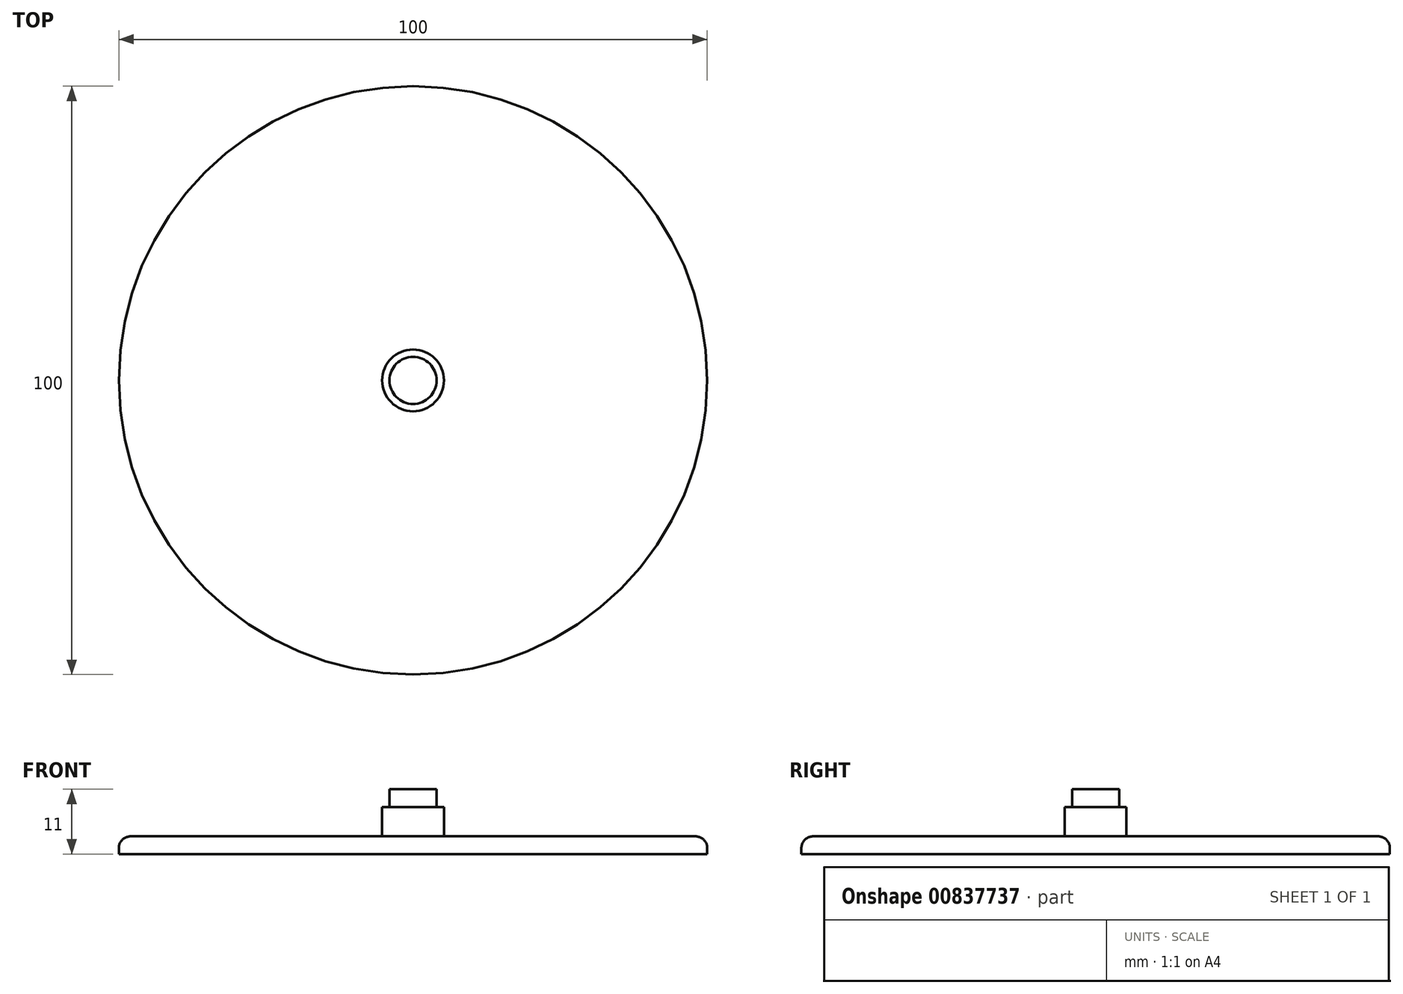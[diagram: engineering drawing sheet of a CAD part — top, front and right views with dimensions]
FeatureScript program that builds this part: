
annotation { "Feature Type Name" : "Feature", "Feature Type Description" : "" }
export const myFeature = defineFeature(function(context is Context, id is Id, definition is map)
    precondition{}
    {
        {
            var Q0;
            Q0=qCreatedBy(makeId("Top.planeOp"),FACE);
            var sketch = newSketch(context, id + "F0", { "sketchPlane" : qUnion([Q0])});
            skCircle(sketch, "E0", {"center": v(0, 0) * mm, "radius": 50 * mm});
            skCircle(sketch, "E1", {"center": v(0, 0) * mm, "radius": 5.25 * mm});
            skCircle(sketch, "E2", {"center": v(0, 0) * mm, "radius": 4 * mm});
            skSolve(sketch);
        }
        {
            var Q0;
            Q0=makeQuery(id+"F0.imprint","IMPRINT",FACE,{"disambiguationData":[TD([[makeQuery(id+"F0.imprint","IMPRINT",EDGE,{"derivedFrom":sQuery(id+"F0.wireOp",EDGE,"E0")}),1.0]])]});
            extrude(context, id + "F1", {"entities" : qUnion([Q0]), "depth" : 3 * mm, "offsetDistance" : 25 * mm});
        }
        {
            var Q0;
            Q0=makeQuery(id+"F0.imprint","IMPRINT",FACE,{"disambiguationData":[TD([[makeQuery(id+"F0.imprint","IMPRINT",EDGE,{"derivedFrom":sQuery(id+"F0.wireOp",EDGE,"E1")}),1.0]])]});
            extrude(context, id + "F2", {"entities" : qUnion([Q0]), "operationType" : NewBodyOperationType.ADD, "depth" : (8) * mm, "offsetDistance" : 25 * mm});
        }
        {
            var Q0;
            Q0=makeQuery(id+"F0.imprint","IMPRINT",FACE,{"disambiguationData":[TD([[makeQuery(id+"F0.imprint","IMPRINT",EDGE,{"derivedFrom":sQuery(id+"F0.wireOp",EDGE,"E2")}),1.0]])]});
            extrude(context, id + "F3", {"entities" : qUnion([Q0]), "operationType" : NewBodyOperationType.ADD, "depth" : 11 * mm, "offsetDistance" : 25 * mm});
        }
        {
            var Q0;
            Q0=makeQuery(id+"F1.opExtrude","CAP_EDGE",EDGE,{"disambiguationData":[OSD([sQuery(id+"F0.wireOp",EDGE,"E0")])],"isStart":false});
            fillet(context, id + "F4", {"entities" : qUnion([Q0]), "radius" : 2 * mm, "tangentPropagation" : true, "allowEdgeOverflow" : false});
        }
    });
